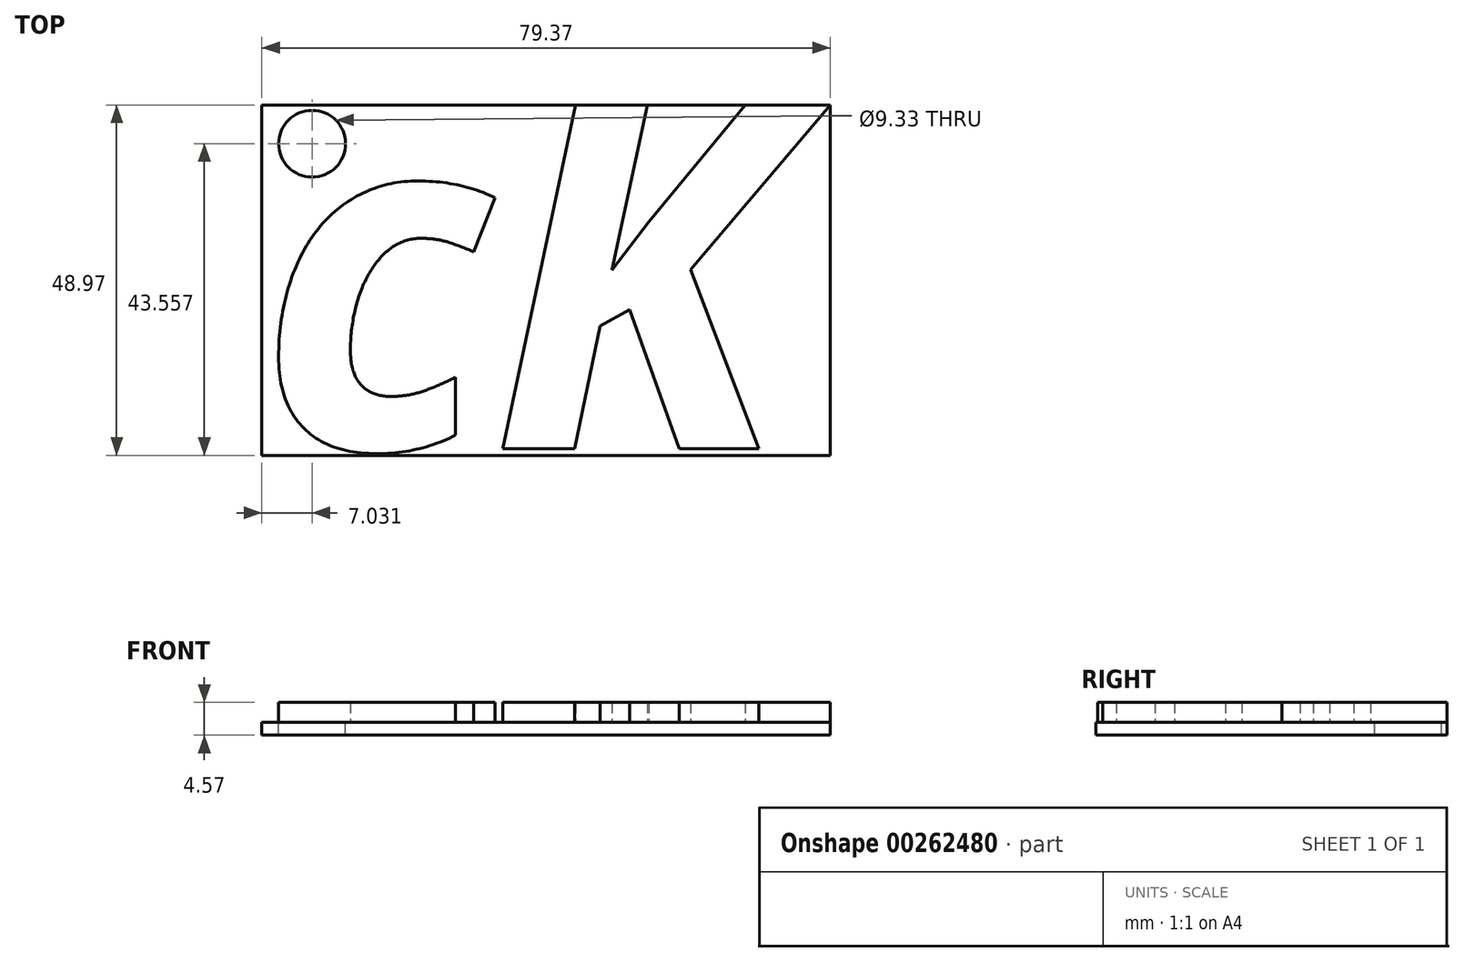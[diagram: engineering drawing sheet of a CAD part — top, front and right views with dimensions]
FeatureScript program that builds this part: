
annotation { "Feature Type Name" : "Feature", "Feature Type Description" : "" }
export const myFeature = defineFeature(function(context is Context, id is Id, definition is map)
    precondition{}
    {
        {
            var Q0;
            Q0=qCreatedBy(makeId("Top.planeOp"),FACE);
            var sketch = newSketch(context, id + "F0", { "sketchPlane" : qUnion([Q0])});
            skText(sketch, "E0", { "text": "cK", "fontName": "OpenSans-BoldItalic.ttf"});
            const initialGuessF0  = {"E0": [-0.0247, -0.03395, 1, 0, 0.04846]};
            skSetInitialGuess(sketch, initialGuessF0);
            skSolve(sketch);
        }
        {
            var Q0;
            Q0 = qSketchRegion(id + "F0", true);
            extrude(context, id + "F1", {"entities" : qUnion([Q0]), "depth" : 2.8 * mm});
        }
        {
            var Q0;
            Q0=makeQuery(id+"F1.opExtrude","CAP_FACE",FACE,{"disambiguationData":[OSD([sQuery(id+"F0.wireOp",EDGE,"E0.sketch_text.stroke-18"),sQuery(id+"F0.wireOp",EDGE,"E0.sketch_text.stroke-19"),sQuery(id+"F0.wireOp",EDGE,"E0.sketch_text.stroke-20"),sQuery(id+"F0.wireOp",EDGE,"E0.sketch_text.stroke-21"),sQuery(id+"F0.wireOp",EDGE,"E0.sketch_text.stroke-22"),sQuery(id+"F0.wireOp",EDGE,"E0.sketch_text.stroke-23"),sQuery(id+"F0.wireOp",EDGE,"E0.sketch_text.stroke-24"),sQuery(id+"F0.wireOp",EDGE,"E0.sketch_text.stroke-25"),sQuery(id+"F0.wireOp",EDGE,"E0.sketch_text.stroke-26"),sQuery(id+"F0.wireOp",EDGE,"E0.sketch_text.stroke-27"),sQuery(id+"F0.wireOp",EDGE,"E0.sketch_text.stroke-28"),sQuery(id+"F0.wireOp",EDGE,"E0.sketch_text.stroke-29"),sQuery(id+"F0.wireOp",EDGE,"E0.sketch_text.stroke-30")])],"isStart":true});
            var sketch = newSketch(context, id + "F2", { "sketchPlane" : qUnion([Q0])});
            skLineSegment(sketch, "E1.bottom", {"start": v(-24.1, 34.87) * mm, "end": v(55.27, 34.87) * mm});
            skLineSegment(sketch, "E1.top", {"start": v(-24.1, -14.1) * mm, "end": v(55.27, -14.1) * mm});
            skLineSegment(sketch, "E1.left", {"start": v(-24.1, 34.87) * mm, "end": v(-24.1, -14.1) * mm});
            skLineSegment(sketch, "E1.right", {"start": v(55.27, 34.87) * mm, "end": v(55.27, -14.1) * mm});
            skCircle(sketch, "E2", {"center": v(-17.07, -8.69) * mm, "radius": 4.66 * mm});
            skLineSegment(sketch, "E3", {"start": v(55.27, 27.64) * mm, "end": v(55.27, 33.95) * mm});
            skLineSegment(sketch, "E4", {"start": v(47.18, 27.64) * mm, "end": v(49.2, 30.8) * mm});
            skLineSegment(sketch, "E5", {"start": v(49.2, 30.8) * mm, "end": v(49.2, 27.64) * mm});
            skLineSegment(sketch, "E6", {"start": v(49.2, 27.64) * mm, "end": v(51.84, 30.8) * mm});
            skPoint(sketch, "E6.endSnap0", {"position": v(55.27, 30.8) * mm});
            skLineSegment(sketch, "E7", {"start": v(51.84, 30.8) * mm, "end": v(51.84, 27.64) * mm});
            skLineSegment(sketch, "E8", {"start": v(51.84, 27.64) * mm, "end": v(55.27, 30.8) * mm});
            skSolve(sketch);
        }
        {
            var Q0;
            Q0 = qSketchRegion(id + "F2", true);
            extrude(context, id + "F3", {"entities" : qUnion([Q0]), "depth" : 1.78 * mm});
        }
    });
